# Revit family: NEVD052LE
name_source: partatom
category: Lighting Fixtures
revit_build: Autodesk Revit 2014 (Build: 20130308_1515(x64)
units: mm (PartAtom-declared; Revit-internal decimal feet)

## types (1)
- NEVD052LED
    Apparent Load = 50 VA
    Assembly Code = D5020200
    Color Filter = 16777215
    Connector Description = Lighting Connector
    Default Elevation = 1219.2 mm  [stored 4 ft]
    Description = The Nevis LED bulkhead delivers an instant bright white light equivalent to a 70W HPS. Designed for low profile applications, the bulkhead can be mounted on walls, handrails and ceilings making it ideal for walkways or restricted height areas. A side mounted increased safety terminal chamber eliminates the need for barrier glands and allows for flush mounting with easy cable access. Its excellent temperature range of -50°C to +55°C makes it a global lighting solution providing high quality lighting at extreme temperatures.
    Dimming Lamp Color Temperature Shift = <None>
    Emit Shape Visible in Rendering = No
    Emit from Circle Diameter = 50 mm  [stored 0.164042 ft]
    Features = Lower power consumption than HID lamps.
Installation to gas groupsIIA and IIB.
Low temperature applications to -55°C.
100,000 maintenance free hours at 25°C (L70).
Highly Energy Efficient.
Compact construction.
    Fixture distribution = Direct
    Glass = Hubbell - Glass
    Height = 535 mm
    Housing Material = Paint - Hubbell - Gray Smooth
    IP Rating = IP66/67
    Inner Length = 200 mm  [stored 0.656168 ft]
    LED Surface = Paint - Hubbell - Light Silver
    Lamp = LED
    Length = 245 mm  [stored 0.803806 ft]
    Load Classification = Lighting
    Manufacturer = Chalmit
    Model = Nevis LED
    Mounting = Paint - Hubbell - Light Silver
    Photometric Web File = CHL_NEVD_052_LE.ies
    Power Factor = 1
    Product Documentation Link = https://hubbellcdn.com
    Product Link = https://www.hubbell.com
    Reflector Finish = Hubbell - White Glass
    Tilt Angle = 90.00°
    URL = https://www.hubbell.com
    Voltage = 120 V
    Warranty = 5 years Warranty
    Wattage Comments = 50W
    Watts = 50 W
    Width = 280 mm  [stored 0.918635 ft]

note: [stored X ft] marks values corroborated as IEEE doubles in the binary element streams (Revit-internal decimal feet)

## geometry (parser evidence)
native form markers: Sweep x2
no freeform markers — native parametric forms only
